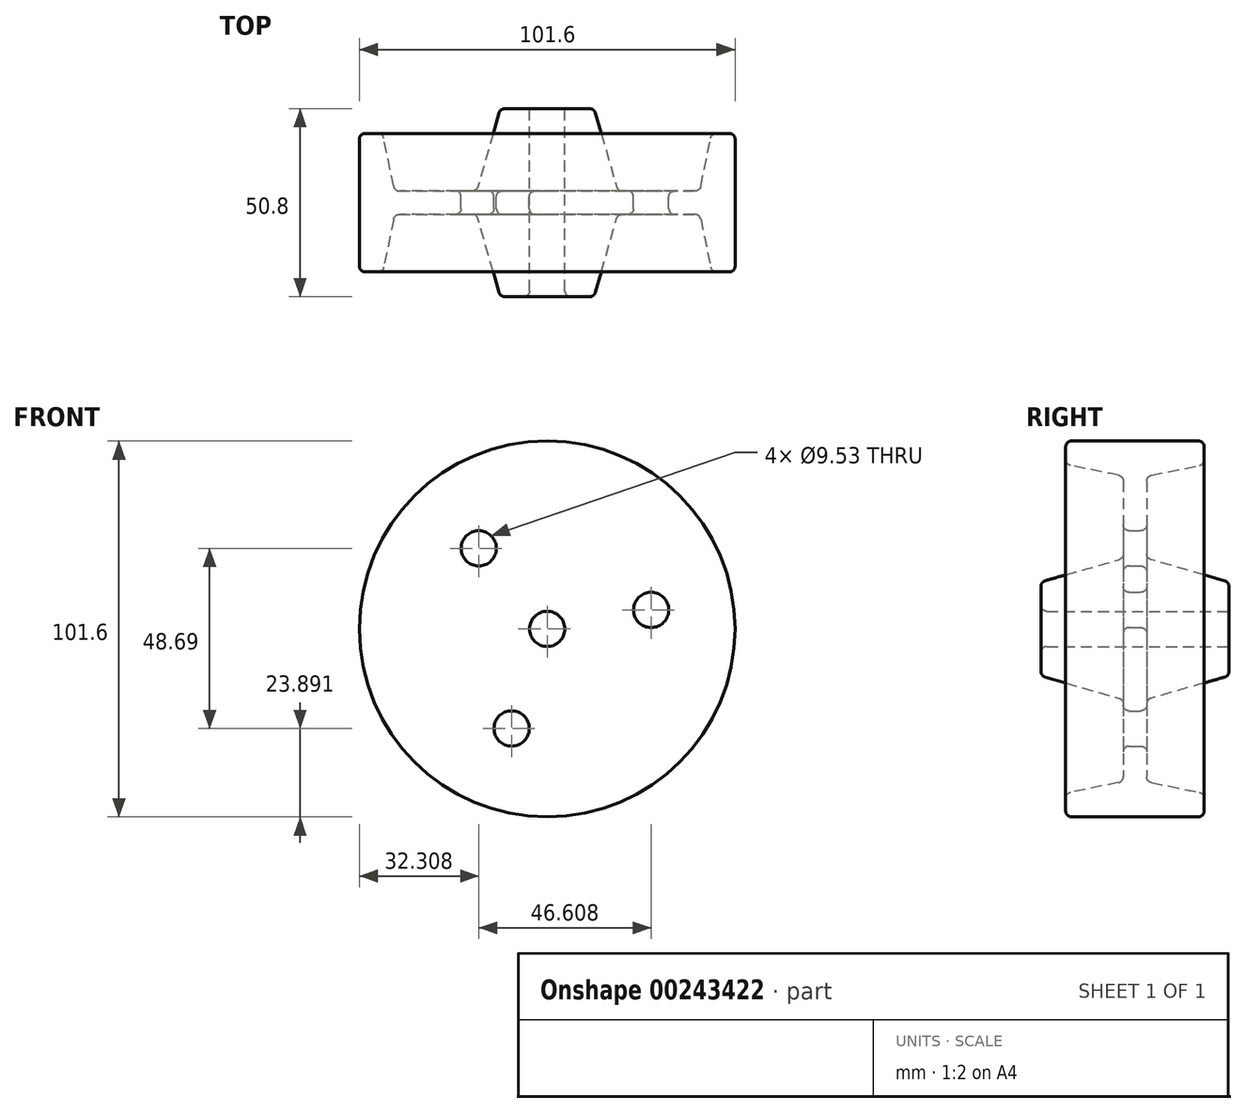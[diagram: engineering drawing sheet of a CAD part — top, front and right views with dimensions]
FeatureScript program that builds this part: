
annotation { "Feature Type Name" : "Feature", "Feature Type Description" : "" }
export const myFeature = defineFeature(function(context is Context, id is Id, definition is map)
    precondition{}
    {
        {
            var Q0;
            Q0=qCreatedBy(makeId("Top.planeOp"),FACE);
            var sketch = newSketch(context, id + "F0", { "sketchPlane" : qUnion([Q0])});
            skLineSegment(sketch, "E0", {"start": v(-29.79, 29.44) * mm, "end": v(-29.79, -21.36) * mm});
            skLineSegment(sketch, "E1", {"start": v(-29.79, -21.36) * mm, "end": v(-17.09, -21.36) * mm});
            skLineSegment(sketch, "E2", {"start": v(-17.09, 29.44) * mm, "end": v(-29.79, 29.44) * mm});
            skLineSegment(sketch, "E3", {"start": v(-17.09, 29.44) * mm, "end": v(-10.73, 7.22) * mm});
            skLineSegment(sketch, "E4", {"start": v(-10.73, 0.87) * mm, "end": v(-17.09, -21.36) * mm});
            skPoint(sketch, "E5.end.orphan", {"position": v(27.7, 29.44) * mm});
            skPoint(sketch, "E6", {"position": v(-29.79, 4.04) * mm});
            skLineSegment(sketch, "E7", {"start": v(21.01, 4.04) * mm, "end": v(21.01, 22.76) * mm});
            skLineSegment(sketch, "E8", {"start": v(21.01, 4.04) * mm, "end": v(21.01, -14.68) * mm});
            skLineSegment(sketch, "E9", {"start": v(21.01, 22.76) * mm, "end": v(14.66, 22.76) * mm});
            skLineSegment(sketch, "E10", {"start": v(-10.73, 7.22) * mm, "end": v(11.49, 7.22) * mm});
            skLineSegment(sketch, "E11", {"start": v(14.66, 22.76) * mm, "end": v(11.49, 7.22) * mm});
            skLineSegment(sketch, "E12", {"start": v(-10.73, 0.87) * mm, "end": v(11.49, 0.87) * mm});
            skLineSegment(sketch, "E13", {"start": v(21.01, 0.87) * mm, "end": v(21.01, -14.68) * mm});
            skLineSegment(sketch, "E14", {"start": v(21.01, -14.68) * mm, "end": v(14.66, -14.68) * mm});
            skLineSegment(sketch, "E15", {"start": v(14.66, -14.68) * mm, "end": v(11.49, 0.87) * mm});
            skSolve(sketch);
        }
        {
            var Q0;
            Q0=makeQuery(id+"F0.imprint","IMPRINT",FACE,{"disambiguationData":[TD([[makeQuery(id+"F0.imprint","IMPRINT",EDGE,{"derivedFrom":sQuery(id+"F0.wireOp",EDGE,"E0")}),1.0]])]});
            var Q1;
            Q1=sQuery(id+"F0.wireOp",EDGE,"E0");
            revolve(context, id + "F1", {"entities" : qUnion([Q0]), "axis" : qUnion([Q1]), "revolveType" : RevolveType.FULL});
        }
        {
            var Q0;
            Q0=makeQuery(id+"F1.opRevolve","SWEPT_FACE",FACE,{"disambiguationData":[OSD([sQuery(id+"F0.wireOp",EDGE,"E2")])]});
            var sketch = newSketch(context, id + "F2", { "sketchPlane" : qUnion([Q0])});
            skCircle(sketch, "E16", {"center": v(29.79, 0) * mm, "radius": 4.76 * mm});
            skCircle(sketch, "E17", {"center": v(48.28, 21.78) * mm, "radius": 4.76 * mm});
            skCircle(sketch, "E18.1.0", {"center": v(1.67, 5.13) * mm, "radius": 4.76 * mm});
            skCircle(sketch, "E18.2.0", {"center": v(39.4, -26.9) * mm, "radius": 4.76 * mm});
            skSolve(sketch);
        }
        {
            var Q0;
            Q0=makeQuery(id+"F2.imprint","IMPRINT",FACE,{"disambiguationData":[TD([[makeQuery(id+"F2.imprint","IMPRINT",EDGE,{"derivedFrom":sQuery(id+"F2.wireOp",EDGE,"E16")}),1.0]])]});
            var Q1;
            Q1=makeQuery(id+"F2.imprint","IMPRINT",FACE,{"disambiguationData":[TD([[makeQuery(id+"F2.imprint","IMPRINT",EDGE,{"derivedFrom":sQuery(id+"F2.wireOp",EDGE,"E18.2.0")}),1.0]])]});
            var Q2;
            Q2=makeQuery(id+"F2.imprint","IMPRINT",FACE,{"disambiguationData":[TD([[makeQuery(id+"F2.imprint","IMPRINT",EDGE,{"derivedFrom":sQuery(id+"F2.wireOp",EDGE,"E17")}),1.0]])]});
            var Q3;
            Q3=makeQuery(id+"F2.imprint","IMPRINT",FACE,{"disambiguationData":[TD([[makeQuery(id+"F2.imprint","IMPRINT",EDGE,{"derivedFrom":sQuery(id+"F2.wireOp",EDGE,"E18.1.0")}),1.0]])]});
            extrude(context, id + "F3", {"entities" : qUnion([Q0, Q1, Q2, Q3]), "operationType" : NewBodyOperationType.REMOVE, "endBound" : BoundingType.THROUGH_ALL, "oppositeDirection" : true, "depth" : 25.4 * mm});
        }
        {
            var Q0;
            Q0=makeQuery(id+"F3.boolean.opBoolean","COPY",EDGE,{"derivedFrom":makeQuery(id+"F3.opExtrude","CAP_EDGE",EDGE,{"disambiguationData":[OSD([sQuery(id+"F2.wireOp",EDGE,"E16")])],"isStart":true})});
            var Q1;
            Q1=makeQuery(id+"F1.opRevolve","SWEPT_EDGE",EDGE,{"disambiguationData":[OSD([sQuery(id+"F0.wireOp",EDGE,"E2"),sQuery(id+"F0.wireOp",EDGE,"E3")])]});
            var Q2;
            Q2=makeQuery(id+"F1.opRevolve","SWEPT_EDGE",EDGE,{"disambiguationData":[OSD([sQuery(id+"F0.wireOp",EDGE,"E3"),sQuery(id+"F0.wireOp",EDGE,"E10")])]});
            var Q3;
            Q3=makeQuery(id+"F3.boolean.opBoolean","INTERSECT",EDGE,{"derivedFrom":[makeQuery(id+"F1.opRevolve","SWEPT_FACE",FACE,{"disambiguationData":[OSD([sQuery(id+"F0.wireOp",EDGE,"E10")])]}),makeQuery(id+"F3.opExtrude","SWEPT_FACE",FACE,{"disambiguationData":[OSD([sQuery(id+"F2.wireOp",EDGE,"E17")])]})]});
            var Q4;
            Q4=makeQuery(id+"F3.boolean.opBoolean","INTERSECT",EDGE,{"derivedFrom":[makeQuery(id+"F1.opRevolve","SWEPT_FACE",FACE,{"disambiguationData":[OSD([sQuery(id+"F0.wireOp",EDGE,"E10")])]}),makeQuery(id+"F3.opExtrude","SWEPT_FACE",FACE,{"disambiguationData":[OSD([sQuery(id+"F2.wireOp",EDGE,"E18.1.0")])]})]});
            var Q5;
            Q5=makeQuery(id+"F3.boolean.opBoolean","INTERSECT",EDGE,{"derivedFrom":[makeQuery(id+"F1.opRevolve","SWEPT_FACE",FACE,{"disambiguationData":[OSD([sQuery(id+"F0.wireOp",EDGE,"E10")])]}),makeQuery(id+"F3.opExtrude","SWEPT_FACE",FACE,{"disambiguationData":[OSD([sQuery(id+"F2.wireOp",EDGE,"E18.2.0")])]})]});
            var Q6;
            Q6=makeQuery(id+"F1.opRevolve","SWEPT_EDGE",EDGE,{"disambiguationData":[OSD([sQuery(id+"F0.wireOp",EDGE,"E10"),sQuery(id+"F0.wireOp",EDGE,"E11")])]});
            var Q7;
            Q7=makeQuery(id+"F1.opRevolve","SWEPT_EDGE",EDGE,{"disambiguationData":[OSD([sQuery(id+"F0.wireOp",EDGE,"E9"),sQuery(id+"F0.wireOp",EDGE,"E11")])]});
            var Q8;
            Q8=makeQuery(id+"F1.opRevolve","SWEPT_EDGE",EDGE,{"disambiguationData":[OSD([sQuery(id+"F0.wireOp",EDGE,"E7"),sQuery(id+"F0.wireOp",EDGE,"E9")])]});
            fillet(context, id + "F4", {"entities" : qUnion([Q0, Q1, Q2, Q3, Q4, Q5, Q6, Q7, Q8]), "radius" : 1.59 * mm, "tangentPropagation" : true, "allowEdgeOverflow" : false});
        }
        {
            var Q0;
            Q0=makeQuery(id+"F3.boolean.opBoolean","INTERSECT",EDGE,{"derivedFrom":[makeQuery(id+"F1.opRevolve","SWEPT_FACE",FACE,{"disambiguationData":[OSD([sQuery(id+"F0.wireOp",EDGE,"E1")])]}),makeQuery(id+"F3.opExtrude","SWEPT_FACE",FACE,{"disambiguationData":[OSD([sQuery(id+"F2.wireOp",EDGE,"E16")])]})]});
            var Q1;
            Q1=makeQuery(id+"F1.opRevolve","SWEPT_EDGE",EDGE,{"disambiguationData":[OSD([sQuery(id+"F0.wireOp",EDGE,"E1"),sQuery(id+"F0.wireOp",EDGE,"E4")])]});
            var Q2;
            Q2=makeQuery(id+"F1.opRevolve","SWEPT_EDGE",EDGE,{"disambiguationData":[OSD([sQuery(id+"F0.wireOp",EDGE,"E4"),sQuery(id+"F0.wireOp",EDGE,"E12")])]});
            var Q3;
            Q3=makeQuery(id+"F3.boolean.opBoolean","INTERSECT",EDGE,{"derivedFrom":[makeQuery(id+"F1.opRevolve","SWEPT_FACE",FACE,{"disambiguationData":[OSD([sQuery(id+"F0.wireOp",EDGE,"E12")])]}),makeQuery(id+"F3.opExtrude","SWEPT_FACE",FACE,{"disambiguationData":[OSD([sQuery(id+"F2.wireOp",EDGE,"E17")])]})]});
            var Q4;
            Q4=makeQuery(id+"F3.boolean.opBoolean","INTERSECT",EDGE,{"derivedFrom":[makeQuery(id+"F1.opRevolve","SWEPT_FACE",FACE,{"disambiguationData":[OSD([sQuery(id+"F0.wireOp",EDGE,"E12")])]}),makeQuery(id+"F3.opExtrude","SWEPT_FACE",FACE,{"disambiguationData":[OSD([sQuery(id+"F2.wireOp",EDGE,"E18.1.0")])]})]});
            var Q5;
            Q5=makeQuery(id+"F3.boolean.opBoolean","INTERSECT",EDGE,{"derivedFrom":[makeQuery(id+"F1.opRevolve","SWEPT_FACE",FACE,{"disambiguationData":[OSD([sQuery(id+"F0.wireOp",EDGE,"E12")])]}),makeQuery(id+"F3.opExtrude","SWEPT_FACE",FACE,{"disambiguationData":[OSD([sQuery(id+"F2.wireOp",EDGE,"E18.2.0")])]})]});
            var Q6;
            Q6=makeQuery(id+"F1.opRevolve","SWEPT_EDGE",EDGE,{"disambiguationData":[OSD([sQuery(id+"F0.wireOp",EDGE,"E12"),sQuery(id+"F0.wireOp",EDGE,"E15")])]});
            var Q7;
            Q7=makeQuery(id+"F1.opRevolve","SWEPT_EDGE",EDGE,{"disambiguationData":[OSD([sQuery(id+"F0.wireOp",EDGE,"E14"),sQuery(id+"F0.wireOp",EDGE,"E15")])]});
            var Q8;
            Q8=makeQuery(id+"F1.opRevolve","SWEPT_EDGE",EDGE,{"disambiguationData":[OSD([sQuery(id+"F0.wireOp",EDGE,"E13"),sQuery(id+"F0.wireOp",EDGE,"E14")])]});
            fillet(context, id + "F5", {"entities" : qUnion([Q0, Q1, Q2, Q3, Q4, Q5, Q6, Q7, Q8]), "radius" : 1.59 * mm, "tangentPropagation" : true, "allowEdgeOverflow" : false});
        }
        {
            var Q0;
            Q0=makeQuery(id+"F1.opRevolve","SWEPT_FACE",FACE,{"disambiguationData":[OSD([sQuery(id+"F0.wireOp",EDGE,"E10")])]});
            var sketch = newSketch(context, id + "F6", { "sketchPlane" : qUnion([Q0])});
            skCircle(sketch, "E19", {"center": v(18.88, 30.63) * mm, "radius": 7.46 * mm});
            skSolve(sketch);
        }
        {
            var Q0;
            Q0=sQuery(id+"F6.wireOp",EDGE,"E19");
            extrude(context, id + "F7", {"bodyType" : ToolBodyType.SURFACE, "surfaceEntities" : qUnion([Q0]), "oppositeDirection" : true, "depth" : 25.4 * mm, "offsetDistance" : 25.4 * mm});
        }
    });
